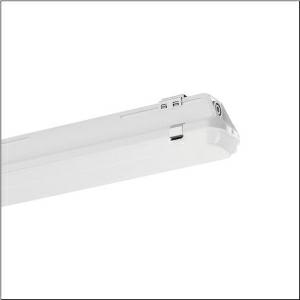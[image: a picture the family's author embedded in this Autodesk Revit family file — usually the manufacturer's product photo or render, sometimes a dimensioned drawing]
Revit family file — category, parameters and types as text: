
# Revit family: monsun_r__11_51fp20ep460l007_261d
name_source: partatom
category: Lighting Fixtures
units: mm (PartAtom-declared; Revit-internal decimal feet)

## family parameters
Cut with Voids When Loaded = No
Host = Face
Light Source = No
Part Type = Normal
Room Calculation Point = No
Round Connector Dimension = Use Diameter
Shared = No

## types (1)
- --- (1 x LED, 5450 lm, 31.5 W, 4000K)
    Apparent Load = 32 VA
    CIE Flux Codes = 45 75 93 94 100
    Color Rendering = 80
    Color Temperature = 4000K
    Default Elevation = 1800 mm
    Description = Monsun® 11, damp-proof luminaire, chain hanger, primary optical cover: enclosure, of PC, light emission: direct distribution, primary light characteristic: symmetric, installation type: suspended mounting, surface-mounted, horizontal mounting, vertical mounting, LED, rated luminous flux: 5.450lm, luminous efficacy: 173lm/W, light colour: 840, colour temperature: 4000K, control gear: DALI 2, with terminal, 5-pole, max. 2.5mm², through-wiring: 7x 2.5mm², mains connection: 220..240V, AC, 50/60Hz, rated input power: 32W, housing, of glass-fibre reinforced polyester, uncoated, bright grey, incl. chain hanger, length: 1.590mm, width: 90mm, height: 88mm, clip for enclosure, of stainless steel (V2A), ceiling mounting element, of stainless steel (V2A), chain hanger, of stainless steel (V2A), protection rating (complete): IP66, insulation class (complete): insulation class I (protective earthing), certification: CE, ENEC, VDE, UKCA, protection symbol: D, impact resistance: IK08, permissible operating ambient temperature: -25..+40°C, standard: EN 50419, EN 60598-2-1, corresponds to IFS (International Featured Standards) requirements for safety and quality in the food industry, for indoor or canopied outdoor use, no direct snow, no direct sun, no direct rain, LABS conformity tested according to VDMA 24364:2018-05, contact your sales advisor before using the luminaires in applications with unclear chemical exposure, large temperature fluctuations or condensation-forming humidity, packaging unit: 1 piece
    Height = 89 mm
    Lamp = 1 x LED
    Lamp Light Flux = 5450 lm
    Lamp Power = 31.5 W
    Lamp count = 1
    Length = 1590 mm
    Luminous efficacy = 173 lm/W
    Manufacturer = Siteco
    ModVariant = No
    Model = 51FP20EP460L007
    Mounting Place = Ceiling
    Mounting Type = Surface mounted
    Number of Poles = 1
    OnlyDefault = Yes
    Power Factor = 1
    Product Name = Monsun® 11
    Product group = damp-proof luminaire
    ProductGroupID = 300
    Protection Class = Protection class I
    Protection Degree = IP 66
    RLX_Detail_Level = 1
    RLX_Emergency_Light_Flux = 0 lm
    RLX_Emergency_Type = 0
    RLX_Emergency_Type_DB = No
    RlxData = <blob elided: 92369 chars, md5=7861e67f>
    Socket = socket
    Standby Power = 0 W
    System Light Flux = 5450 lm
    System Power = 32 W
    Type Comments = factory setting: luminous flux: 100 % | dim-lin: 254 | 219 mA
    Type Image = l_1349237.jpg
    URL = http://relux.com
    VarID = @adj_018142
    Voltage = 0 V
    Weight = 0.00 kg
    Width = 90 mm

## geometry (parser evidence)
native form markers: Blend x4, Sweep x14
no freeform markers — native parametric forms only
